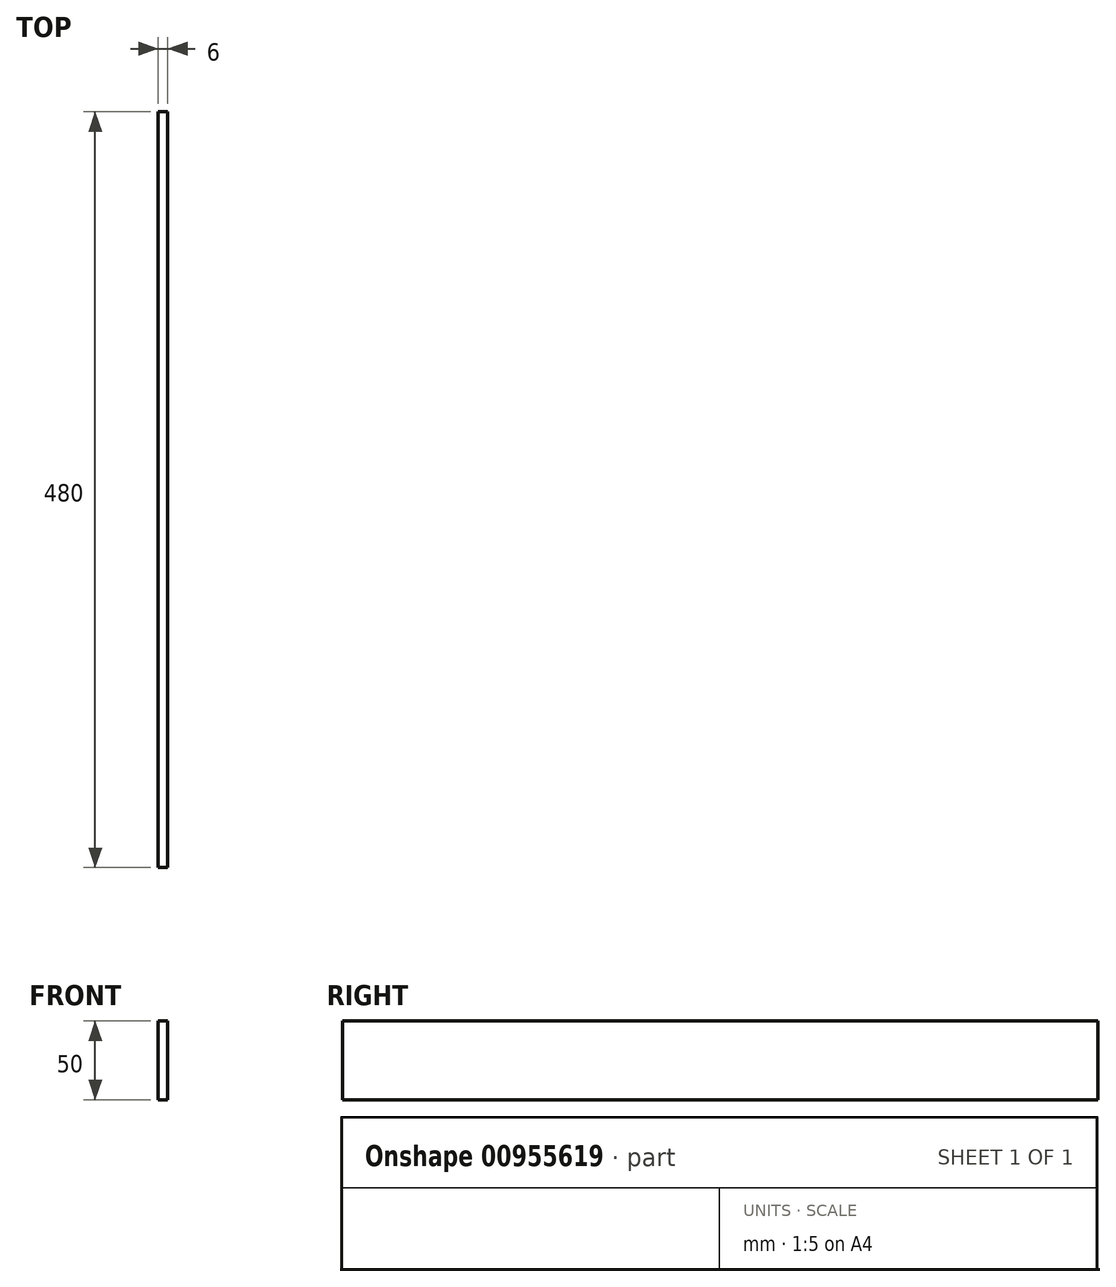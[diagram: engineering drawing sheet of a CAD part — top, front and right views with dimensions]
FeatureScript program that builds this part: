
annotation { "Feature Type Name" : "Feature", "Feature Type Description" : "" }
export const myFeature = defineFeature(function(context is Context, id is Id, definition is map)
    precondition{}
    {
        {
            var Q0;
            Q0=qCreatedBy(makeId("Front.planeOp"),FACE);
            var sketch = newSketch(context, id + "F0", { "sketchPlane" : qUnion([Q0])});
            skLineSegment(sketch, "E0.bottom", {"start": v(0, 0) * mm, "end": v(6, 0) * mm});
            skLineSegment(sketch, "E0.top", {"start": v(0, 50) * mm, "end": v(6, 50) * mm});
            skLineSegment(sketch, "E0.left", {"start": v(0, 0) * mm, "end": v(0, 50) * mm});
            skLineSegment(sketch, "E0.right", {"start": v(6, 0) * mm, "end": v(6, 50) * mm});
            skSolve(sketch);
        }
        {
            var Q0;
            Q0 = qSketchRegion(id + "F0", true);
            extrude(context, id + "F1", {"entities" : qUnion([Q0]), "depth" : 480 * mm, "offsetDistance" : 25 * mm});
        }
    });
